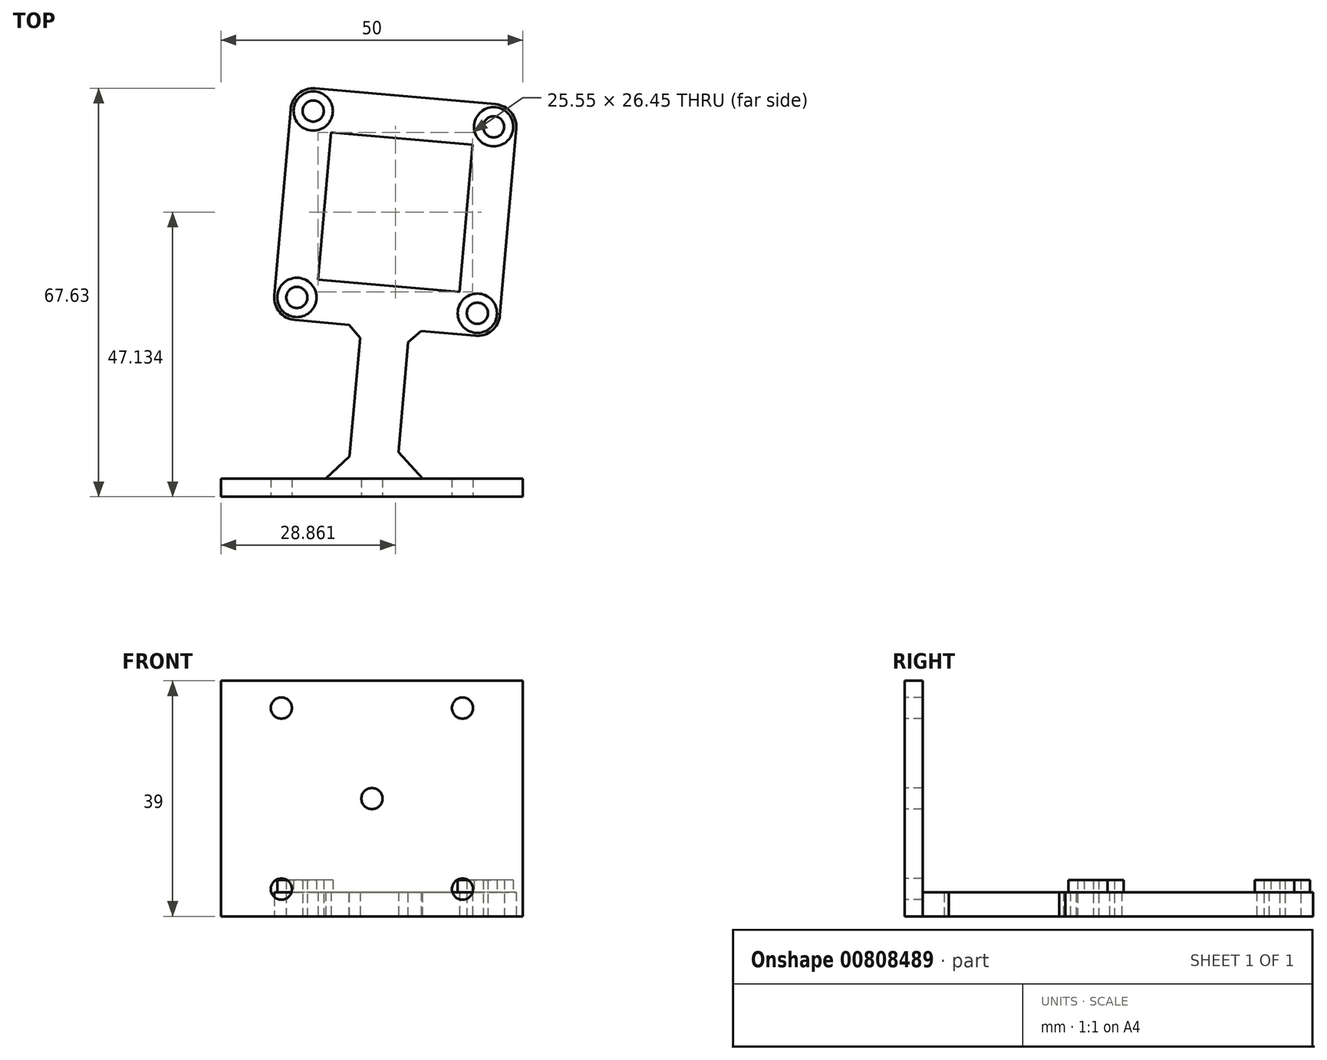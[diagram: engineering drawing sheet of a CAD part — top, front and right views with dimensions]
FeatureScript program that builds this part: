
annotation { "Feature Type Name" : "Feature", "Feature Type Description" : "" }
export const myFeature = defineFeature(function(context is Context, id is Id, definition is map)
    precondition{}
    {
        {
            var Q0;
            Q0=qCreatedBy(makeId("Top.planeOp"),FACE);
            var sketch = newSketch(context, id + "F0", { "sketchPlane" : qUnion([Q0])});
            skLineSegment(sketch, "E0.bottom", {"start": v(-25, 1.5) * mm, "end": v(25, 1.5) * mm});
            skLineSegment(sketch, "E0.top", {"start": v(-25, -1.5) * mm, "end": v(25, -1.5) * mm});
            skLineSegment(sketch, "E0.left", {"start": v(-25, 1.5) * mm, "end": v(-25, -1.5) * mm});
            skLineSegment(sketch, "E0.right", {"start": v(25, 1.5) * mm, "end": v(25, -1.5) * mm});
            skPoint(sketch, "E0.middle", {"position": v(0, 0) * mm});
            skLineSegment(sketch, "E1", {"start": v(-4.02, 1.5) * mm, "end": v(-1.47, 30.54) * mm});
            skLineSegment(sketch, "E2", {"start": v(-1.47, 30.54) * mm, "end": v(6.5, 29.84) * mm});
            skLineSegment(sketch, "E3", {"start": v(6.5, 29.84) * mm, "end": v(4.02, 1.5) * mm});
            skLineSegment(sketch, "E4", {"start": v(-9.73, 62.38) * mm, "end": v(20.16, 59.77) * mm, "construction": true});
            skLineSegment(sketch, "E5", {"start": v(20.16, 59.77) * mm, "end": v(17.45, 28.89) * mm, "construction": true});
            skLineSegment(sketch, "E6", {"start": v(17.45, 28.89) * mm, "end": v(-12.43, 31.5) * mm, "construction": true});
            skLineSegment(sketch, "E7", {"start": v(-12.43, 31.5) * mm, "end": v(-9.73, 62.38) * mm, "construction": true});
            skCircle(sketch, "E8", {"center": v(-12.43, 31.5) * mm, "radius": 1.75 * mm});
            skCircle(sketch, "E9", {"center": v(17.45, 28.89) * mm, "radius": 1.75 * mm});
            skCircle(sketch, "E10", {"center": v(-9.73, 62.38) * mm, "radius": 1.75 * mm});
            skCircle(sketch, "E11", {"center": v(20.16, 59.77) * mm, "radius": 1.75 * mm});
            skCircle(sketch, "E12", {"center": v(20.16, 59.77) * mm, "radius": 3.75 * mm});
            skCircle(sketch, "E13", {"center": v(-9.73, 62.38) * mm, "radius": 3.75 * mm});
            skCircle(sketch, "E14", {"center": v(-12.43, 31.5) * mm, "radius": 3.75 * mm});
            skCircle(sketch, "E15", {"center": v(17.45, 28.89) * mm, "radius": 3.75 * mm});
            skPoint(sketch, "E16", {"position": v(2.51, 30.2) * mm});
            skLineSegment(sketch, "E17", {"start": v(-13.47, 62.7) * mm, "end": v(-16.17, 31.83) * mm});
            skLineSegment(sketch, "E18", {"start": v(-12.76, 27.76) * mm, "end": v(17.13, 25.15) * mm});
            skLineSegment(sketch, "E19", {"start": v(21.19, 28.56) * mm, "end": v(23.9, 59.44) * mm});
            skLineSegment(sketch, "E20", {"start": v(20.48, 63.5) * mm, "end": v(-9.4, 66.12) * mm});
            skLineSegment(sketch, "E21", {"start": v(-6.78, 58.86) * mm, "end": v(-8.91, 34.45) * mm});
            skLineSegment(sketch, "E22", {"start": v(-8.91, 34.45) * mm, "end": v(14.5, 32.4) * mm});
            skLineSegment(sketch, "E23", {"start": v(14.5, 32.4) * mm, "end": v(16.63, 56.81) * mm});
            skLineSegment(sketch, "E24", {"start": v(16.63, 56.81) * mm, "end": v(-6.78, 58.86) * mm});
            skLineSegment(sketch, "E25", {"start": v(2.51, 30.2) * mm, "end": v(0, 1.5) * mm, "construction": true});
            skPoint(sketch, "E26", {"position": v(0, 1.5) * mm});
            skSolve(sketch);
        }
        {
            var Q0;
            Q0 = qSketchRegion(id + "F0", true);
            extrude(context, id + "F1", {"entities" : qUnion([Q0]), "depth" : 4 * mm, "offsetDistance" : 25 * mm});
        }
        {
            var Q0;
            Q0=makeQuery(id+"F1.opExtrude","CAP_FACE",FACE,{"disambiguationData":[OSD([sQuery(id+"F0.wireOp",EDGE,"E0.bottom"),sQuery(id+"F0.wireOp",EDGE,"E0.top"),sQuery(id+"F0.wireOp",EDGE,"E0.left"),sQuery(id+"F0.wireOp",EDGE,"E0.right"),sQuery(id+"F0.wireOp",EDGE,"E1"),sQuery(id+"F0.wireOp",EDGE,"E3"),sQuery(id+"F0.wireOp",EDGE,"E8"),sQuery(id+"F0.wireOp",EDGE,"E9"),sQuery(id+"F0.wireOp",EDGE,"E10"),sQuery(id+"F0.wireOp",EDGE,"E11"),sQuery(id+"F0.wireOp",EDGE,"E12"),sQuery(id+"F0.wireOp",EDGE,"E13"),sQuery(id+"F0.wireOp",EDGE,"E14"),sQuery(id+"F0.wireOp",EDGE,"E15"),sQuery(id+"F0.wireOp",EDGE,"E17"),sQuery(id+"F0.wireOp",EDGE,"E18"),sQuery(id+"F0.wireOp",EDGE,"E19"),sQuery(id+"F0.wireOp",EDGE,"E20"),sQuery(id+"F0.wireOp",EDGE,"E21"),sQuery(id+"F0.wireOp",EDGE,"E22"),sQuery(id+"F0.wireOp",EDGE,"E23"),sQuery(id+"F0.wireOp",EDGE,"E24")])],"isStart":false});
            var sketch = newSketch(context, id + "F2", { "sketchPlane" : qUnion([Q0])});
            skLineSegment(sketch, "E27.bottom", {"start": v(-25, 1.5) * mm, "end": v(25, 1.5) * mm});
            skLineSegment(sketch, "E27.top", {"start": v(-25, -1.5) * mm, "end": v(25, -1.5) * mm});
            skLineSegment(sketch, "E27.left", {"start": v(-25, 1.5) * mm, "end": v(-25, -1.5) * mm});
            skLineSegment(sketch, "E27.right", {"start": v(25, 1.5) * mm, "end": v(25, -1.5) * mm});
            skSolve(sketch);
        }
        {
            var Q0;
            Q0 = qSketchRegion(id + "F2", true);
            extrude(context, id + "F3", {"entities" : qUnion([Q0]), "operationType" : NewBodyOperationType.ADD, "depth" : 35 * mm, "offsetDistance" : 25 * mm});
        }
        {
            var Q0;
            Q0=makeQuery(id+"F3.boolean.opBoolean","MERGE",FACE,{"derivedFrom":[makeQuery(id+"F1.opExtrude","SWEPT_FACE",FACE,{"disambiguationData":[OSD([sQuery(id+"F0.wireOp",EDGE,"E0.top")])]}),makeQuery(id+"F3.opExtrude","SWEPT_FACE",FACE,{"disambiguationData":[OSD([sQuery(id+"F2.wireOp",EDGE,"E27.top")])]})]});
            var sketch = newSketch(context, id + "F4", { "sketchPlane" : qUnion([Q0])});
            skLineSegment(sketch, "E28", {"start": v(0, 39) * mm, "end": v(0, 0) * mm, "construction": true});
            skLineSegment(sketch, "E29", {"start": v(-25, 19.5) * mm, "end": v(25, 19.5) * mm, "construction": true});
            skLineSegment(sketch, "E30.bottom", {"start": v(-15, 34.5) * mm, "end": v(15, 34.5) * mm, "construction": true});
            skLineSegment(sketch, "E30.top", {"start": v(-15, 4.5) * mm, "end": v(15, 4.5) * mm, "construction": true});
            skLineSegment(sketch, "E30.left", {"start": v(-15, 34.5) * mm, "end": v(-15, 4.5) * mm, "construction": true});
            skLineSegment(sketch, "E30.right", {"start": v(15, 34.5) * mm, "end": v(15, 4.5) * mm, "construction": true});
            skPoint(sketch, "E30.middle", {"position": v(0, 19.5) * mm});
            skCircle(sketch, "E31", {"center": v(-15, 34.5) * mm, "radius": 1.75 * mm});
            skCircle(sketch, "E32", {"center": v(15, 34.5) * mm, "radius": 1.75 * mm});
            skCircle(sketch, "E33", {"center": v(-15, 4.5) * mm, "radius": 1.75 * mm});
            skCircle(sketch, "E34", {"center": v(15, 4.5) * mm, "radius": 1.75 * mm});
            skCircle(sketch, "E35", {"center": v(0, 19.5) * mm, "radius": 1.75 * mm});
            skSolve(sketch);
        }
        {
            var Q0;
            Q0 = qSketchRegion(id + "F4", true);
            var Q1;
            {var subQ0=sQuery(id+"F0.wireOp",EDGE,"E0.bottom");Q1=makeQuery(id+"F3.boolean.opBoolean","MERGE",FACE,{"derivedFrom":[makeQuery(id+"F1.opExtrude","SWEPT_FACE",FACE,{"disambiguationData":[OSD([subQ0]),TDD([makeQuery(id+"F0.imprint","IMPRINT",EDGE,{"disambiguationData":[TD([[makeQuery(id+"F0.imprint","INTERSECT",VERTEX,{"derivedFrom":[subQ0,sQuery(id+"F0.wireOp",EDGE,"E0.left")]}),-1.0]])],"derivedFrom":subQ0})])]}),makeQuery(id+"F1.opExtrude","SWEPT_FACE",FACE,{"disambiguationData":[OSD([subQ0]),TDD([makeQuery(id+"F0.imprint","IMPRINT",EDGE,{"disambiguationData":[TD([[makeQuery(id+"F0.imprint","INTERSECT",VERTEX,{"derivedFrom":[subQ0,sQuery(id+"F0.wireOp",EDGE,"E0.right")]}),1.0]])],"derivedFrom":subQ0})])]}),makeQuery(id+"F3.opExtrude","SWEPT_FACE",FACE,{"disambiguationData":[OSD([sQuery(id+"F2.wireOp",EDGE,"E27.bottom")])]})]});}
            extrude(context, id + "F5", {"entities" : qUnion([Q0]), "operationType" : NewBodyOperationType.REMOVE, "endBound" : BoundingType.UP_TO_SURFACE, "oppositeDirection" : true, "depth" : 25 * mm, "endBoundEntityFace" : qUnion([Q1]), "offsetDistance" : 25 * mm});
        }
        {
            var Q0;
            Q0=makeQuery(id+"F3.opExtrude","CAP_EDGE",EDGE,{"disambiguationData":[OSD([sQuery(id+"F2.wireOp",EDGE,"E27.bottom")])],"isStart":true});
            var Q1;
            Q1=makeQuery(id+"F1.opExtrude","SWEPT_EDGE",EDGE,{"disambiguationData":[OSD([sQuery(id+"F0.wireOp",EDGE,"E0.bottom"),sQuery(id+"F0.wireOp",EDGE,"E1")])]});
            var Q2;
            Q2=makeQuery(id+"F1.opExtrude","SWEPT_EDGE",EDGE,{"disambiguationData":[OSD([sQuery(id+"F0.wireOp",EDGE,"E0.bottom"),sQuery(id+"F0.wireOp",EDGE,"E3")])]});
            chamfer(context, id + "F6", {"entities" : qUnion([Q0, Q1, Q2]), "width" : 4 * mm, "tangentPropagation" : true});
        }
        {
            var Q0;
            Q0=makeQuery(id+"F1.opExtrude","CAP_FACE",FACE,{"disambiguationData":[OSD([sQuery(id+"F0.wireOp",EDGE,"E0.bottom"),sQuery(id+"F0.wireOp",EDGE,"E0.top"),sQuery(id+"F0.wireOp",EDGE,"E0.left"),sQuery(id+"F0.wireOp",EDGE,"E0.right"),sQuery(id+"F0.wireOp",EDGE,"E1"),sQuery(id+"F0.wireOp",EDGE,"E3"),sQuery(id+"F0.wireOp",EDGE,"E8"),sQuery(id+"F0.wireOp",EDGE,"E9"),sQuery(id+"F0.wireOp",EDGE,"E10"),sQuery(id+"F0.wireOp",EDGE,"E11"),sQuery(id+"F0.wireOp",EDGE,"E12"),sQuery(id+"F0.wireOp",EDGE,"E13"),sQuery(id+"F0.wireOp",EDGE,"E14"),sQuery(id+"F0.wireOp",EDGE,"E15"),sQuery(id+"F0.wireOp",EDGE,"E17"),sQuery(id+"F0.wireOp",EDGE,"E18"),sQuery(id+"F0.wireOp",EDGE,"E19"),sQuery(id+"F0.wireOp",EDGE,"E20"),sQuery(id+"F0.wireOp",EDGE,"E21"),sQuery(id+"F0.wireOp",EDGE,"E22"),sQuery(id+"F0.wireOp",EDGE,"E23"),sQuery(id+"F0.wireOp",EDGE,"E24")])],"isStart":false});
            var sketch = newSketch(context, id + "F7", { "sketchPlane" : qUnion([Q0])});
            skLineSegment(sketch, "E36.0.0", {"start": v(-1.8, 26.8) * mm, "end": v(-3.67, 5.5) * mm});
            skLineSegment(sketch, "E36.0.1", {"start": v(-3.67, 5.5) * mm, "end": v(4.72, 5.5) * mm});
            skLineSegment(sketch, "E36.0.2", {"start": v(4.72, 5.5) * mm, "end": v(4.4, 5.85) * mm});
            skLineSegment(sketch, "E36.0.3", {"start": v(4.4, 5.85) * mm, "end": v(6.17, 26.1) * mm});
            skLineSegment(sketch, "E36.0.4", {"start": v(6.17, 26.1) * mm, "end": v(17.13, 25.15) * mm});
            skArc(sketch, "E36.0.5", {"start": v(17.13, 25.15) * mm, "mid": v(19.86, 26.01) * mm, "end": v(21.19, 28.56) * mm});
            skLineSegment(sketch, "E36.0.6", {"start": v(21.19, 28.56) * mm, "end": v(23.9, 59.44) * mm});
            skArc(sketch, "E36.0.7", {"start": v(23.9, 59.44) * mm, "mid": v(23.03, 62.18) * mm, "end": v(20.48, 63.5) * mm});
            skLineSegment(sketch, "E36.0.8", {"start": v(20.48, 63.5) * mm, "end": v(-9.4, 66.12) * mm});
            skArc(sketch, "E36.0.9", {"start": v(-9.4, 66.12) * mm, "mid": v(-12.14, 65.25) * mm, "end": v(-13.47, 62.7) * mm});
            skLineSegment(sketch, "E36.0.10", {"start": v(-13.47, 62.7) * mm, "end": v(-16.17, 31.83) * mm});
            skArc(sketch, "E36.0.11", {"start": v(-16.17, 31.83) * mm, "mid": v(-15.3, 29.09) * mm, "end": v(-12.76, 27.76) * mm});
            skLineSegment(sketch, "E36.0.12", {"start": v(-12.76, 27.76) * mm, "end": v(-1.8, 26.8) * mm});
            skCircle(sketch, "E37", {"center": v(-12.43, 31.5) * mm, "radius": 3.25 * mm});
            skCircle(sketch, "E38", {"center": v(17.45, 28.89) * mm, "radius": 3.25 * mm});
            skCircle(sketch, "E39", {"center": v(-9.73, 62.38) * mm, "radius": 3.25 * mm});
            skCircle(sketch, "E40", {"center": v(20.16, 59.77) * mm, "radius": 3.25 * mm});
            skCircle(sketch, "E41.0", {"center": v(-9.73, 62.38) * mm, "radius": 1.75 * mm});
            skCircle(sketch, "E42.0", {"center": v(20.16, 59.77) * mm, "radius": 1.75 * mm});
            skCircle(sketch, "E43.0", {"center": v(17.45, 28.89) * mm, "radius": 1.75 * mm});
            skCircle(sketch, "E44.0", {"center": v(-12.43, 31.5) * mm, "radius": 1.75 * mm});
            skSolve(sketch);
        }
        {
            var Q0;
            Q0=makeQuery(id+"F7.imprint","IMPRINT",FACE,{"disambiguationData":[TD([[makeQuery(id+"F7.imprint","IMPRINT",EDGE,{"derivedFrom":sQuery(id+"F7.wireOp",EDGE,"E39")}),1.0]])]});
            var Q1;
            Q1=makeQuery(id+"F7.imprint","IMPRINT",FACE,{"disambiguationData":[TD([[makeQuery(id+"F7.imprint","IMPRINT",EDGE,{"derivedFrom":sQuery(id+"F7.wireOp",EDGE,"E40")}),1.0]])]});
            var Q2;
            Q2=makeQuery(id+"F7.imprint","IMPRINT",FACE,{"disambiguationData":[TD([[makeQuery(id+"F7.imprint","IMPRINT",EDGE,{"derivedFrom":sQuery(id+"F7.wireOp",EDGE,"E38")}),1.0]])]});
            var Q3;
            Q3=makeQuery(id+"F7.imprint","IMPRINT",FACE,{"disambiguationData":[TD([[makeQuery(id+"F7.imprint","IMPRINT",EDGE,{"derivedFrom":sQuery(id+"F7.wireOp",EDGE,"E37")}),1.0]])]});
            extrude(context, id + "F8", {"entities" : qUnion([Q0, Q1, Q2, Q3]), "operationType" : NewBodyOperationType.ADD, "depth" : 2 * mm, "offsetDistance" : 25 * mm});
        }
        {
            var Q0;
            Q0=makeQuery(id+"F1.opExtrude","SWEPT_EDGE",EDGE,{"disambiguationData":[OSD([sQuery(id+"F0.wireOp",EDGE,"E3"),sQuery(id+"F0.wireOp",EDGE,"E18")])]});
            var Q1;
            Q1=makeQuery(id+"F1.opExtrude","SWEPT_EDGE",EDGE,{"disambiguationData":[OSD([sQuery(id+"F0.wireOp",EDGE,"E1"),sQuery(id+"F0.wireOp",EDGE,"E18")])]});
            chamfer(context, id + "F9", {"entities" : qUnion([Q0, Q1]), "width" : 2 * mm, "tangentPropagation" : true});
        }
    });
